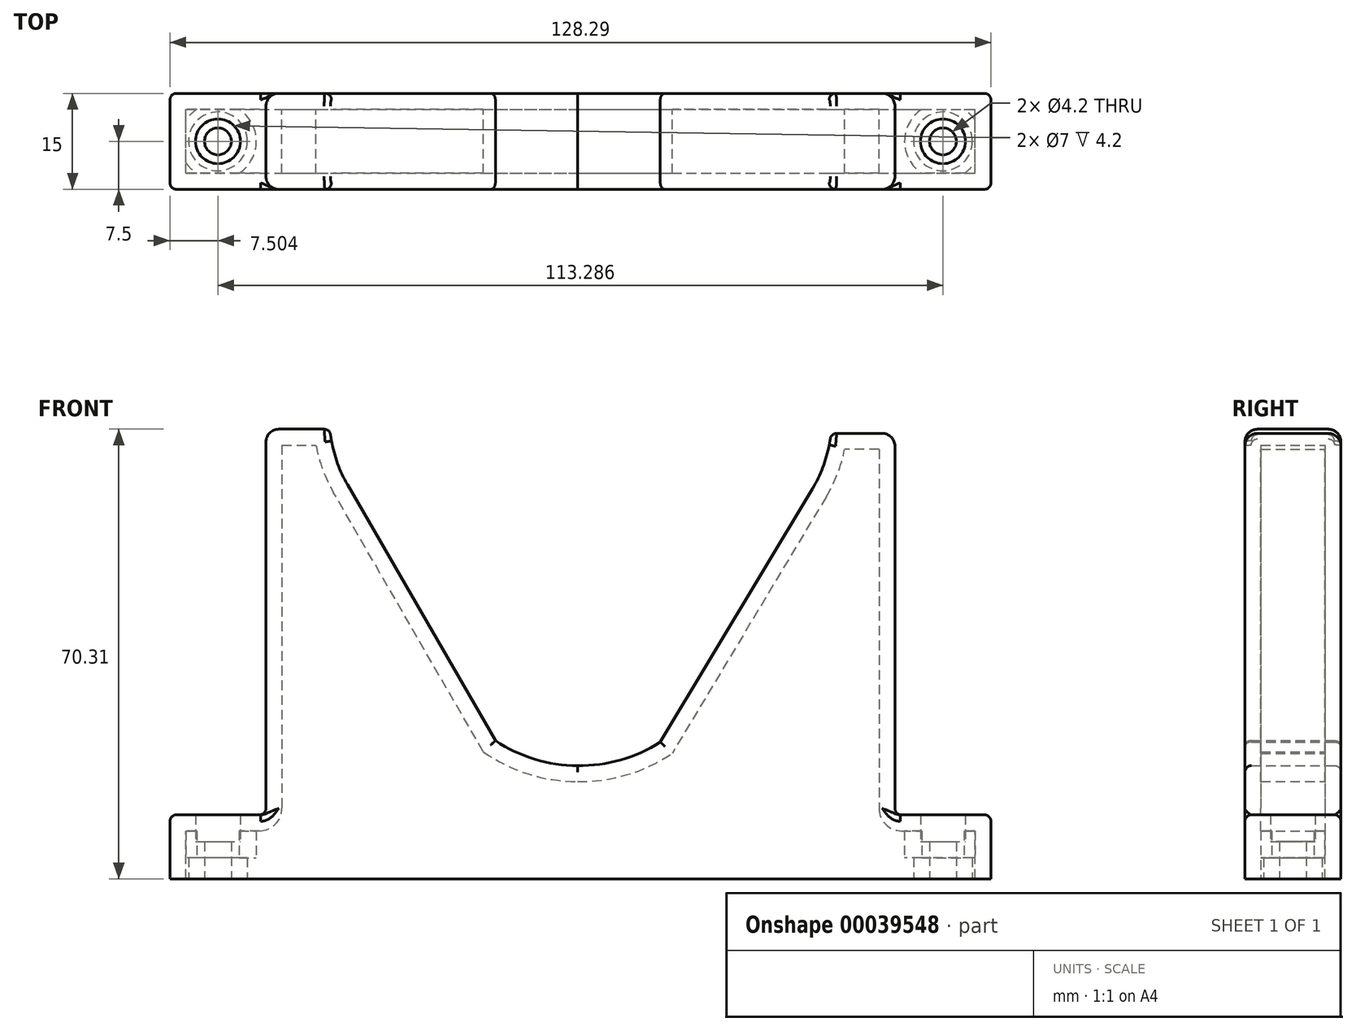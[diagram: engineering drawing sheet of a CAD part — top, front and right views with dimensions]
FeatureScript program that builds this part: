
annotation { "Feature Type Name" : "Feature", "Feature Type Description" : "" }
export const myFeature = defineFeature(function(context is Context, id is Id, definition is map)
    precondition{}
    {
        {
            var Q0;
            Q0=qCreatedBy(makeId("Front.planeOp"),FACE);
            var sketch = newSketch(context, id + "F0", { "sketchPlane" : qUnion([Q0])});
            skArc(sketch, "E0.5", {"start": v(-35.07, 29.34) * mm, "mid": v(-34.17, 24.85) * mm, "end": v(-32.33, 20.67) * mm});
            skLineSegment(sketch, "E0.6", {"start": v(-32.33, 20.67) * mm, "end": v(-9.22, -19.37) * mm});
            skArc(sketch, "E0.7", {"start": v(-9.22, -19.37) * mm, "mid": v(-3.08, -22.27) * mm, "end": v(3.64, -23.27) * mm});
            skLineSegment(sketch, "E1", {"start": v(54.25, 51.84) * mm, "end": v(54.25, 51.52) * mm});
            skArc(sketch, "E2.MirrorCS", {"start": v(16.55, -19.59) * mm, "mid": v(10.37, -22.39) * mm, "end": v(3.64, -23.27) * mm});
            skLineSegment(sketch, "E3.MirrorCS", {"start": v(40.34, 20.05) * mm, "end": v(16.55, -19.59) * mm});
            skArc(sketch, "E4.MirrorCS", {"start": v(43.22, 28.67) * mm, "mid": v(42.25, 24.2) * mm, "end": v(40.34, 20.05) * mm});
            skLineSegment(sketch, "E5", {"start": v(-35.07, 29.34) * mm, "end": v(-45.07, 29.34) * mm});
            skLineSegment(sketch, "E6", {"start": v(-45.07, 29.34) * mm, "end": v(-45.07, -40.97) * mm});
            skLineSegment(sketch, "E7", {"start": v(43.22, 28.67) * mm, "end": v(53.22, 28.67) * mm});
            skLineSegment(sketch, "E8", {"start": v(53.22, 28.67) * mm, "end": v(53.22, -40.97) * mm});
            skLineSegment(sketch, "E9", {"start": v(53.22, -40.97) * mm, "end": v(68.22, -40.97) * mm});
            skLineSegment(sketch, "E10", {"start": v(68.22, -40.97) * mm, "end": v(68.22, -30.97) * mm});
            skLineSegment(sketch, "E11", {"start": v(68.22, -30.97) * mm, "end": v(53.22, -30.97) * mm});
            skLineSegment(sketch, "E12", {"start": v(-45.07, -40.97) * mm, "end": v(-60.07, -40.97) * mm});
            skLineSegment(sketch, "E13", {"start": v(-60.07, -40.97) * mm, "end": v(-60.07, -30.97) * mm});
            skLineSegment(sketch, "E14", {"start": v(-60.07, -30.97) * mm, "end": v(-45.07, -30.97) * mm});
            skLineSegment(sketch, "E15", {"start": v(53.22, -40.97) * mm, "end": v(-45.07, -40.97) * mm});
            skSolve(sketch);
        }
        {
            var Q0;
            {var subQ1=sQuery(id+"F0.wireOp",EDGE,"E9");Q0=makeQuery(id+"F0.imprint","IMPRINT",FACE,{"disambiguationData":[TD([[makeQuery(id+"F0.imprint","IMPRINT",EDGE,{"derivedFrom":subQ1}),1.0]])]});}
            var Q1;
            Q1=makeQuery(id+"F0.imprint","IMPRINT",FACE,{"disambiguationData":[TD([[makeQuery(id+"F0.imprint","IMPRINT",EDGE,{"derivedFrom":sQuery(id+"F0.wireOp",EDGE,"E0.5")}),-1.0]])]});
            var Q2;
            {var subQ1=sQuery(id+"F0.wireOp",EDGE,"E12");Q2=makeQuery(id+"F0.imprint","IMPRINT",FACE,{"disambiguationData":[TD([[makeQuery(id+"F0.imprint","IMPRINT",EDGE,{"derivedFrom":subQ1}),-1.0]])]});}
            extrude(context, id + "F1", {"entities" : qUnion([Q0, Q1, Q2]), "depth" : 15 * mm});
        }
        {
            var Q0;
            Q0=makeQuery(id+"F1.opExtrude","SWEPT_FACE",FACE,{"disambiguationData":[OSD([sQuery(id+"F0.wireOp",EDGE,"E14")])]});
            var sketch = newSketch(context, id + "F2", { "sketchPlane" : qUnion([Q0])});
            skLineSegment(sketch, "E16", {"start": v(-52.57, 0) * mm, "end": v(-52.57, -15) * mm});
            skLineSegment(sketch, "E17", {"start": v(-60.07, -7.5) * mm, "end": v(-52.57, -7.5) * mm});
            skSolve(sketch);
        }
        {
            var Q0;
            Q0=sQuery(id+"F2.wireOp",VERTEX,"E17.end");
            var Q1;
            Q1=makeQuery(id+"F1.opExtrude","SWEPT_BODY",BODY,{"disambiguationData":[OSD([sQuery(id+"F0.wireOp",EDGE,"E0.5"),sQuery(id+"F0.wireOp",EDGE,"E0.6"),sQuery(id+"F0.wireOp",EDGE,"E0.7"),sQuery(id+"F0.wireOp",EDGE,"E2.MirrorCS"),sQuery(id+"F0.wireOp",EDGE,"E3.MirrorCS"),sQuery(id+"F0.wireOp",EDGE,"E4.MirrorCS"),sQuery(id+"F0.wireOp",EDGE,"E5"),sQuery(id+"F0.wireOp",EDGE,"E6"),sQuery(id+"F0.wireOp",EDGE,"E7"),sQuery(id+"F0.wireOp",EDGE,"E8"),sQuery(id+"F0.wireOp",EDGE,"E9"),sQuery(id+"F0.wireOp",EDGE,"E10"),sQuery(id+"F0.wireOp",EDGE,"E11"),sQuery(id+"F0.wireOp",EDGE,"E12"),sQuery(id+"F0.wireOp",EDGE,"E13"),sQuery(id+"F0.wireOp",EDGE,"E14"),sQuery(id+"F0.wireOp",EDGE,"E15")])]});
            hole(context, id + "F3", {"style" : HoleStyle.C_BORE, "holeDiameter" : 4.2 * mm, "cBoreDiameter" : 7 * mm, "cBoreDepth" : 4.2 * mm, "endStyle" : HoleEndStyle.THROUGH, "locations" : qUnion([Q0]), "scope" : qUnion([Q1])});
        }
        {
            var Q0;
            Q0=makeQuery(id+"F1.opExtrude","SWEPT_FACE",FACE,{"disambiguationData":[OSD([sQuery(id+"F0.wireOp",EDGE,"E11")])]});
            var sketch = newSketch(context, id + "F4", { "sketchPlane" : qUnion([Q0])});
            skLineSegment(sketch, "E18", {"start": v(60.72, 0) * mm, "end": v(60.72, -15) * mm});
            skLineSegment(sketch, "E19", {"start": v(60.72, -7.5) * mm, "end": v(53.22, -7.5) * mm});
            skSolve(sketch);
        }
        {
            var Q0;
            Q0=sQuery(id+"F4.wireOp",VERTEX,"E19.start");
            var Q1;
            Q1=makeQuery(id+"F1.opExtrude","SWEPT_BODY",BODY,{"disambiguationData":[OSD([sQuery(id+"F0.wireOp",EDGE,"E0.5"),sQuery(id+"F0.wireOp",EDGE,"E0.6"),sQuery(id+"F0.wireOp",EDGE,"E0.7"),sQuery(id+"F0.wireOp",EDGE,"E2.MirrorCS"),sQuery(id+"F0.wireOp",EDGE,"E3.MirrorCS"),sQuery(id+"F0.wireOp",EDGE,"E4.MirrorCS"),sQuery(id+"F0.wireOp",EDGE,"E5"),sQuery(id+"F0.wireOp",EDGE,"E6"),sQuery(id+"F0.wireOp",EDGE,"E7"),sQuery(id+"F0.wireOp",EDGE,"E8"),sQuery(id+"F0.wireOp",EDGE,"E9"),sQuery(id+"F0.wireOp",EDGE,"E10"),sQuery(id+"F0.wireOp",EDGE,"E11"),sQuery(id+"F0.wireOp",EDGE,"E12"),sQuery(id+"F0.wireOp",EDGE,"E13"),sQuery(id+"F0.wireOp",EDGE,"E14"),sQuery(id+"F0.wireOp",EDGE,"E15")])]});
            hole(context, id + "F5", {"style" : HoleStyle.C_BORE, "holeDiameter" : 4.2 * mm, "cBoreDiameter" : 7 * mm, "cBoreDepth" : 4.2 * mm, "endStyle" : HoleEndStyle.THROUGH, "locations" : qUnion([Q0]), "scope" : qUnion([Q1])});
        }
        {
            var Q0;
            Q0=makeQuery(id+"F1.opExtrude","CAP_EDGE",EDGE,{"disambiguationData":[OSD([sQuery(id+"F0.wireOp",EDGE,"E8")])],"isStart":true});
            var Q1;
            Q1=makeQuery(id+"F1.opExtrude","CAP_EDGE",EDGE,{"disambiguationData":[OSD([sQuery(id+"F0.wireOp",EDGE,"E8")])],"isStart":false});
            var Q2;
            Q2=makeQuery(id+"F1.opExtrude","CAP_EDGE",EDGE,{"disambiguationData":[OSD([sQuery(id+"F0.wireOp",EDGE,"E7")])],"isStart":true});
            var Q3;
            Q3=makeQuery(id+"F1.opExtrude","SWEPT_EDGE",EDGE,{"disambiguationData":[OSD([sQuery(id+"F0.wireOp",EDGE,"E7"),sQuery(id+"F0.wireOp",EDGE,"E8")])]});
            var Q4;
            Q4=makeQuery(id+"F1.opExtrude","CAP_EDGE",EDGE,{"disambiguationData":[OSD([sQuery(id+"F0.wireOp",EDGE,"E7")])],"isStart":false});
            var Q5;
            Q5=makeQuery(id+"F1.opExtrude","CAP_EDGE",EDGE,{"disambiguationData":[OSD([sQuery(id+"F0.wireOp",EDGE,"E5")])],"isStart":true});
            var Q6;
            Q6=makeQuery(id+"F1.opExtrude","SWEPT_EDGE",EDGE,{"disambiguationData":[OSD([sQuery(id+"F0.wireOp",EDGE,"E5"),sQuery(id+"F0.wireOp",EDGE,"E6")])]});
            var Q7;
            Q7=makeQuery(id+"F1.opExtrude","CAP_EDGE",EDGE,{"disambiguationData":[OSD([sQuery(id+"F0.wireOp",EDGE,"E5")])],"isStart":false});
            var Q8;
            Q8=makeQuery(id+"F1.opExtrude","CAP_EDGE",EDGE,{"disambiguationData":[OSD([sQuery(id+"F0.wireOp",EDGE,"E6")])],"isStart":true});
            var Q9;
            Q9=makeQuery(id+"F1.opExtrude","CAP_EDGE",EDGE,{"disambiguationData":[OSD([sQuery(id+"F0.wireOp",EDGE,"E6")])],"isStart":false});
            fillet(context, id + "F6", {"entities" : qUnion([Q0, Q1, Q2, Q3, Q4, Q5, Q6, Q7, Q8, Q9]), "radius" : 2 * mm, "tangentPropagation" : true, "allowEdgeOverflow" : false});
        }
        {
            var Q0;
            Q0=makeQuery(id+"F1.opExtrude","CAP_EDGE",EDGE,{"disambiguationData":[OSD([sQuery(id+"F0.wireOp",EDGE,"E11")])],"isStart":true});
            var Q1;
            Q1=makeQuery(id+"F1.opExtrude","CAP_EDGE",EDGE,{"disambiguationData":[OSD([sQuery(id+"F0.wireOp",EDGE,"E11")])],"isStart":false});
            var Q2;
            Q2=makeQuery(id+"F1.opExtrude","SWEPT_EDGE",EDGE,{"disambiguationData":[OSD([sQuery(id+"F0.wireOp",EDGE,"E10"),sQuery(id+"F0.wireOp",EDGE,"E11")])]});
            var Q3;
            {var subQ0=sQuery(id+"F0.wireOp",EDGE,"E8");Q3=makeQuery(id+"F6.opFillet","BLEND_EDGE",EDGE,{"blendedFrom":[makeQuery(id+"F1.opExtrude","CAP_EDGE",EDGE,{"disambiguationData":[OSD([subQ0])],"isStart":true}),makeQuery(id+"F1.opExtrude","CAP_FACE",FACE,{"disambiguationData":[OSD([sQuery(id+"F0.wireOp",EDGE,"E0.5"),sQuery(id+"F0.wireOp",EDGE,"E0.6"),sQuery(id+"F0.wireOp",EDGE,"E0.7"),sQuery(id+"F0.wireOp",EDGE,"E2.MirrorCS"),sQuery(id+"F0.wireOp",EDGE,"E3.MirrorCS"),sQuery(id+"F0.wireOp",EDGE,"E4.MirrorCS"),sQuery(id+"F0.wireOp",EDGE,"E5"),sQuery(id+"F0.wireOp",EDGE,"E6"),sQuery(id+"F0.wireOp",EDGE,"E7"),subQ0,sQuery(id+"F0.wireOp",EDGE,"E9"),sQuery(id+"F0.wireOp",EDGE,"E10"),sQuery(id+"F0.wireOp",EDGE,"E11"),sQuery(id+"F0.wireOp",EDGE,"E12"),sQuery(id+"F0.wireOp",EDGE,"E13"),sQuery(id+"F0.wireOp",EDGE,"E14"),sQuery(id+"F0.wireOp",EDGE,"E15")])],"isStart":true})],"blendedInto":[makeQuery(id+"F1.opExtrude","CAP_FACE",FACE,{"disambiguationData":[OSD([sQuery(id+"F0.wireOp",EDGE,"E0.5"),sQuery(id+"F0.wireOp",EDGE,"E0.6"),sQuery(id+"F0.wireOp",EDGE,"E0.7"),sQuery(id+"F0.wireOp",EDGE,"E2.MirrorCS"),sQuery(id+"F0.wireOp",EDGE,"E3.MirrorCS"),sQuery(id+"F0.wireOp",EDGE,"E4.MirrorCS"),sQuery(id+"F0.wireOp",EDGE,"E5"),sQuery(id+"F0.wireOp",EDGE,"E6"),sQuery(id+"F0.wireOp",EDGE,"E7"),subQ0,sQuery(id+"F0.wireOp",EDGE,"E9"),sQuery(id+"F0.wireOp",EDGE,"E10"),sQuery(id+"F0.wireOp",EDGE,"E11"),sQuery(id+"F0.wireOp",EDGE,"E12"),sQuery(id+"F0.wireOp",EDGE,"E13"),sQuery(id+"F0.wireOp",EDGE,"E14"),sQuery(id+"F0.wireOp",EDGE,"E15")])],"isStart":true})]});}
            var Q4;
            Q4=makeQuery(id+"F1.opExtrude","CAP_EDGE",EDGE,{"disambiguationData":[OSD([sQuery(id+"F0.wireOp",EDGE,"E10")])],"isStart":true});
            var Q5;
            Q5=makeQuery(id+"F1.opExtrude","CAP_EDGE",EDGE,{"disambiguationData":[OSD([sQuery(id+"F0.wireOp",EDGE,"E13")])],"isStart":true});
            var Q6;
            Q6=makeQuery(id+"F1.opExtrude","CAP_EDGE",EDGE,{"disambiguationData":[OSD([sQuery(id+"F0.wireOp",EDGE,"E14")])],"isStart":true});
            var Q7;
            Q7=makeQuery(id+"F1.opExtrude","CAP_EDGE",EDGE,{"disambiguationData":[OSD([sQuery(id+"F0.wireOp",EDGE,"E14")])],"isStart":false});
            var Q8;
            Q8=makeQuery(id+"F1.opExtrude","SWEPT_EDGE",EDGE,{"disambiguationData":[OSD([sQuery(id+"F0.wireOp",EDGE,"E13"),sQuery(id+"F0.wireOp",EDGE,"E14")])]});
            var Q9;
            Q9=makeQuery(id+"F1.opExtrude","CAP_EDGE",EDGE,{"disambiguationData":[OSD([sQuery(id+"F0.wireOp",EDGE,"E13")])],"isStart":false});
            var Q10;
            Q10=makeQuery(id+"F1.opExtrude","SWEPT_EDGE",EDGE,{"disambiguationData":[OSD([sQuery(id+"F0.wireOp",EDGE,"E6"),sQuery(id+"F0.wireOp",EDGE,"E14")])]});
            var Q11;
            Q11=makeQuery(id+"F1.opExtrude","CAP_EDGE",EDGE,{"disambiguationData":[OSD([sQuery(id+"F0.wireOp",EDGE,"E10")])],"isStart":false});
            var Q12;
            Q12=makeQuery(id+"F1.opExtrude","SWEPT_EDGE",EDGE,{"disambiguationData":[OSD([sQuery(id+"F0.wireOp",EDGE,"E8"),sQuery(id+"F0.wireOp",EDGE,"E11")])]});
            var Q13;
            Q13=makeQuery(id+"F1.opExtrude","CAP_EDGE",EDGE,{"disambiguationData":[OSD([sQuery(id+"F0.wireOp",EDGE,"E2.MirrorCS")])],"isStart":false});
            var Q14;
            Q14=makeQuery(id+"F1.opExtrude","CAP_EDGE",EDGE,{"disambiguationData":[OSD([sQuery(id+"F0.wireOp",EDGE,"E0.7")])],"isStart":false});
            var Q15;
            Q15=makeQuery(id+"F1.opExtrude","CAP_EDGE",EDGE,{"disambiguationData":[OSD([sQuery(id+"F0.wireOp",EDGE,"E0.6")])],"isStart":false});
            var Q16;
            Q16=makeQuery(id+"F1.opExtrude","CAP_EDGE",EDGE,{"disambiguationData":[OSD([sQuery(id+"F0.wireOp",EDGE,"E0.6")])],"isStart":true});
            var Q17;
            Q17=makeQuery(id+"F1.opExtrude","CAP_EDGE",EDGE,{"disambiguationData":[OSD([sQuery(id+"F0.wireOp",EDGE,"E0.7")])],"isStart":true});
            var Q18;
            Q18=makeQuery(id+"F1.opExtrude","CAP_EDGE",EDGE,{"disambiguationData":[OSD([sQuery(id+"F0.wireOp",EDGE,"E2.MirrorCS")])],"isStart":true});
            var Q19;
            Q19=makeQuery(id+"F1.opExtrude","CAP_EDGE",EDGE,{"disambiguationData":[OSD([sQuery(id+"F0.wireOp",EDGE,"E4.MirrorCS")])],"isStart":false});
            fillet(context, id + "F7", {"entities" : qUnion([Q0, Q1, Q2, Q3, Q4, Q5, Q6, Q7, Q8, Q9, Q10, Q11, Q12, Q13, Q14, Q15, Q16, Q17, Q18, Q19]), "radius" : 1 * mm, "tangentPropagation" : true, "allowEdgeOverflow" : false});
        }
        {
            var Q0;
            Q0=makeQuery(id+"F1.opExtrude","SWEPT_FACE",FACE,{"disambiguationData":[OSD([sQuery(id+"F0.wireOp",EDGE,"E9"),sQuery(id+"F0.wireOp",EDGE,"E12"),sQuery(id+"F0.wireOp",EDGE,"E15")])]});
            shell(context, id + "F8", {"entities" : qUnion([Q0]), "thickness" : 2.5 * mm});
        }
    });
